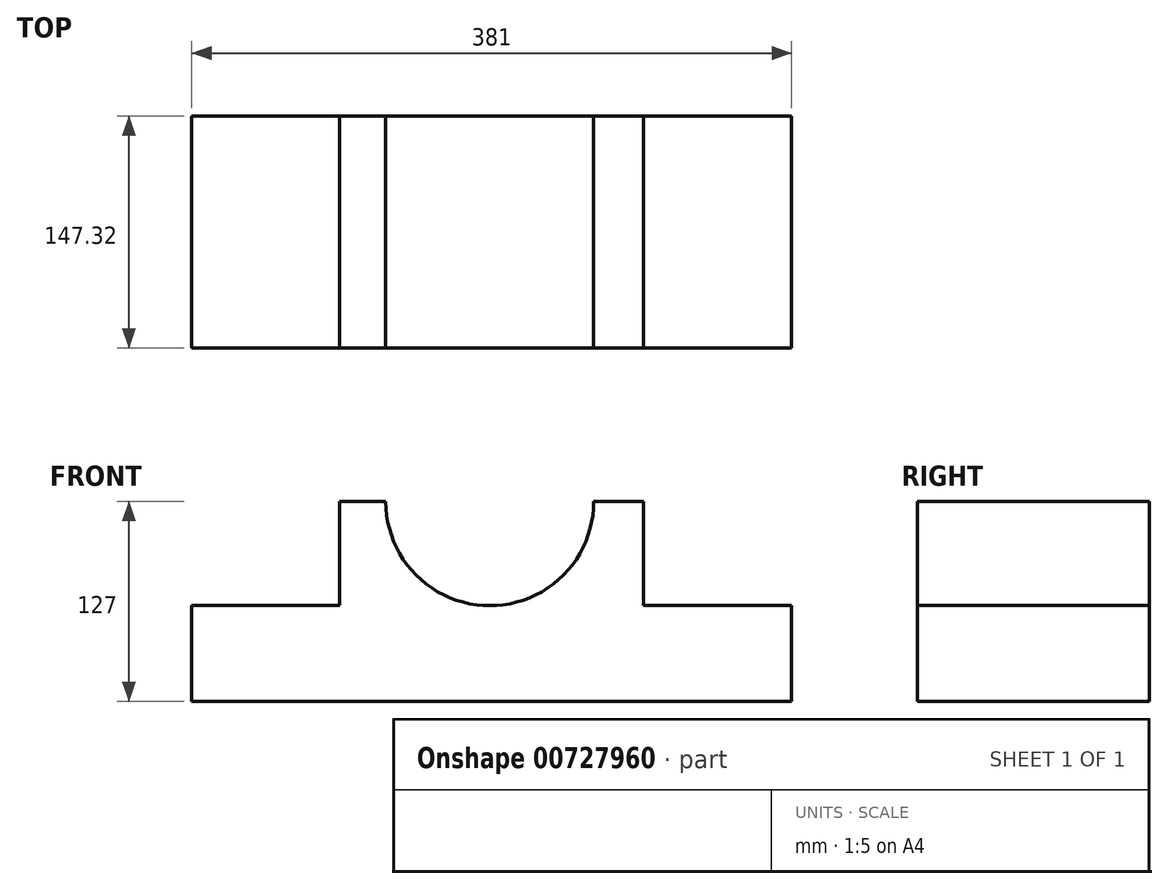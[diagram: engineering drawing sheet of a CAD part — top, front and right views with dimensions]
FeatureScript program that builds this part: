
annotation { "Feature Type Name" : "Feature", "Feature Type Description" : "" }
export const myFeature = defineFeature(function(context is Context, id is Id, definition is map)
    precondition{}
    {
        {
            var Q0;
            Q0=qCreatedBy(makeId("Front.planeOp"),FACE);
            var sketch = newSketch(context, id + "F0", { "sketchPlane" : qUnion([Q0])});
            skLineSegment(sketch, "E0.bottom", {"start": v(-93.98, 30.14) * mm, "end": v(287.02, 30.14) * mm});
            skLineSegment(sketch, "E0.top", {"start": v(-93.98, -30.82) * mm, "end": v(287.02, -30.82) * mm});
            skLineSegment(sketch, "E0.left", {"start": v(-93.98, 30.14) * mm, "end": v(-93.98, -30.82) * mm});
            skLineSegment(sketch, "E0.right", {"start": v(287.02, 30.14) * mm, "end": v(287.02, -30.82) * mm});
            skLineSegment(sketch, "E1.bottom", {"start": v(0, 30.14) * mm, "end": v(193.04, 30.14) * mm});
            skLineSegment(sketch, "E1.top", {"start": v(0, 96.18) * mm, "end": v(193.04, 96.18) * mm});
            skLineSegment(sketch, "E1.left", {"start": v(0, 30.14) * mm, "end": v(0, 96.18) * mm});
            skLineSegment(sketch, "E1.right", {"start": v(193.04, 30.14) * mm, "end": v(193.04, 96.18) * mm});
            skArc(sketch, "E2", {"start": v(29.21, 96.18) * mm, "mid": v(95.25, 30) * mm, "end": v(161.3, 96.18) * mm});
            skSolve(sketch);
        }
        {
            var Q0;
            Q0=makeQuery(id+"F0.imprint","IMPRINT",FACE,{"disambiguationData":[TD([[makeQuery(id+"F0.imprint","IMPRINT",EDGE,{"derivedFrom":sQuery(id+"F0.wireOp",EDGE,"E0.top")}),1.0]])]});
            var Q1;
            {var subQ0=sQuery(id+"F0.wireOp",EDGE,"E1.left");Q1=makeQuery(id+"F0.imprint","IMPRINT",FACE,{"disambiguationData":[TD([[makeQuery(id+"F0.imprint","IMPRINT",EDGE,{"derivedFrom":subQ0}),-1.0]])]});}
            var Q2;
            {var subQ0=sQuery(id+"F0.wireOp",EDGE,"E1.right");Q2=makeQuery(id+"F0.imprint","IMPRINT",FACE,{"disambiguationData":[TD([[makeQuery(id+"F0.imprint","IMPRINT",EDGE,{"derivedFrom":subQ0}),1.0]])]});}
            extrude(context, id + "F1", {"entities" : qUnion([Q0, Q1, Q2]), "depth" : 147.32 * mm, "offsetDistance" : 25.4 * mm});
        }
    });
